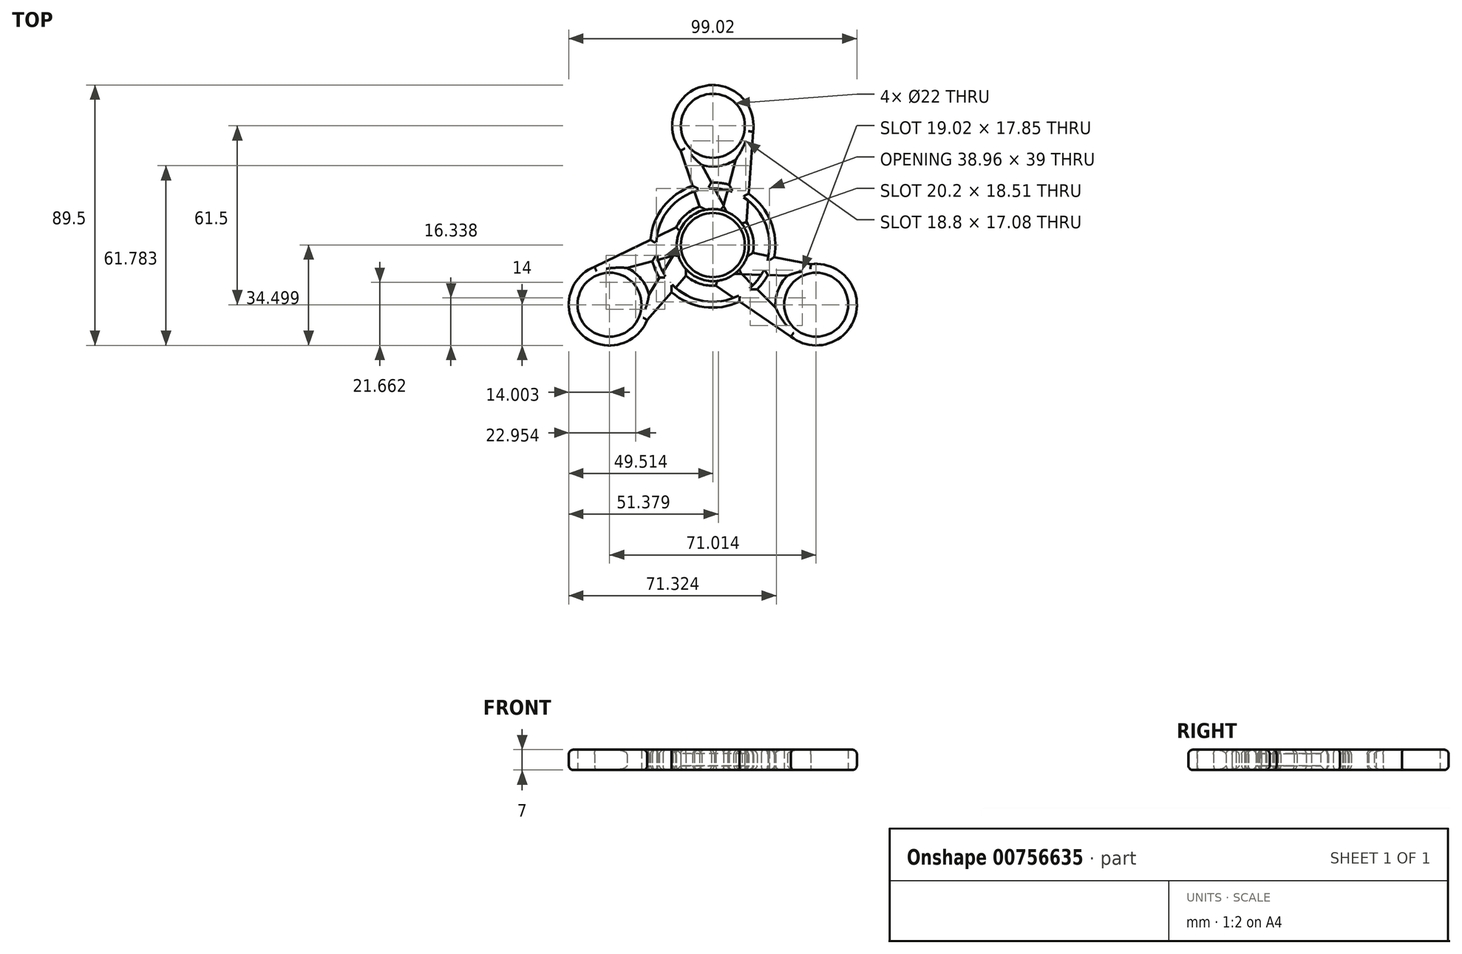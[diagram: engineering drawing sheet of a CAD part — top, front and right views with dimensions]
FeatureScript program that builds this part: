
annotation { "Feature Type Name" : "Feature", "Feature Type Description" : "" }
export const myFeature = defineFeature(function(context is Context, id is Id, definition is map)
    precondition{}
    {
        {
            var Q0;
            Q0=qCreatedBy(makeId("Top.planeOp"),FACE);
            var sketch = newSketch(context, id + "F0", { "sketchPlane" : qUnion([Q0])});
            skLineSegment(sketch, "E0.bottom", {"start": v(-14, 55) * mm, "end": v(14, 55) * mm});
            skLineSegment(sketch, "E0.top", {"start": v(-14, -14) * mm, "end": v(14, -14) * mm});
            skLineSegment(sketch, "E0.left", {"start": v(-14, 55) * mm, "end": v(-14, -14) * mm});
            skLineSegment(sketch, "E0.right", {"start": v(14, 55) * mm, "end": v(14, -14) * mm});
            skCircle(sketch, "E1", {"center": v(0, 0) * mm, "radius": 14 * mm});
            skCircle(sketch, "E2", {"center": v(0, 41) * mm, "radius": 14 * mm});
            skCircle(sketch, "E3", {"center": v(0, 0) * mm, "radius": 11 * mm});
            skCircle(sketch, "E4", {"center": v(0, 41) * mm, "radius": 11 * mm});
            skLineSegment(sketch, "E5", {"start": v(-14, 41) * mm, "end": v(14, 41) * mm});
            skLineSegment(sketch, "E6", {"start": v(-14, 0) * mm, "end": v(14, 0) * mm});
            skLineSegment(sketch, "E7", {"start": v(0, 41) * mm, "end": v(0, 0) * mm});
            skPoint(sketch, "E8", {"position": v(0, 11) * mm});
            skCircle(sketch, "E9", {"center": v(0, 0) * mm, "radius": 21.5 * mm});
            skCircle(sketch, "E10", {"center": v(0, 0) * mm, "radius": 19.5 * mm});
            skLineSegment(sketch, "E11", {"start": v(0, 21.5) * mm, "end": v(0, 19.5) * mm});
            skLineSegment(sketch, "E12", {"start": v(-14, 41) * mm, "end": v(0, 0) * mm});
            skLineSegment(sketch, "E13", {"start": v(-11, 41) * mm, "end": v(11, 0) * mm});
            skLineSegment(sketch, "E14", {"start": v(11, 41) * mm, "end": v(0, 0) * mm});
            skLineSegment(sketch, "E15", {"start": v(11, 0) * mm, "end": v(14, 41) * mm});
            skSolve(sketch);
        }
        {
            var Q0;
            {var subQ0=sQuery(id+"F0.wireOp",EDGE,"iO3ZXdYe-Cxbd-9ZMA-kq9E-F6ahPa86oXzm.right");var subQ1=sQuery(id+"F0.wireOp",EDGE,"E1");var subQ2=makeQuery(id+"F0.imprint","INTERSECT",VERTEX,{"derivedFrom":[subQ1,subQ0]});Q0=makeQuery(id+"F0.imprint","IMPRINT",FACE,{"disambiguationData":[TD([[makeQuery(id+"F0.imprint","IMPRINT",EDGE,{"disambiguationData":[TD([[subQ2,-1.0]])],"derivedFrom":subQ1}),1.0]])]});}
            var Q1;
            {var subQ0=sQuery(id+"F0.wireOp",EDGE,"E7");var subQ1=sQuery(id+"F0.wireOp",EDGE,"E2");var subQ2=makeQuery(id+"F0.imprint","INTERSECT",VERTEX,{"derivedFrom":[subQ1,subQ0]});Q1=makeQuery(id+"F0.imprint","IMPRINT",FACE,{"disambiguationData":[TD([[makeQuery(id+"F0.imprint","IMPRINT",EDGE,{"disambiguationData":[TD([[subQ2,-1.0]])],"derivedFrom":subQ1}),1.0]])]});}
            var Q2;
            {var subQ0=sQuery(id+"F0.wireOp",EDGE,"iO3ZXdYe-Cxbd-9ZMA-kq9E-F6ahPa86oXzm.right");var subQ1=sQuery(id+"F0.wireOp",EDGE,"E1");var subQ2=makeQuery(id+"F0.imprint","INTERSECT",VERTEX,{"derivedFrom":[subQ1,subQ0]});Q2=makeQuery(id+"F0.imprint","IMPRINT",FACE,{"disambiguationData":[TD([[makeQuery(id+"F0.imprint","IMPRINT",EDGE,{"disambiguationData":[TD([[subQ2,-1.0]])],"derivedFrom":subQ1}),-1.0]])]});}
            var Q3;
            {var subQ0=sQuery(id+"F0.wireOp",EDGE,"E9");var subQ1=sQuery(id+"F0.wireOp",EDGE,"iO3ZXdYe-Cxbd-9ZMA-kq9E-F6ahPa86oXzm.right");var subQ2=makeQuery(id+"F0.imprint","INTERSECT",VERTEX,{"derivedFrom":[subQ1,subQ0]});Q3=makeQuery(id+"F0.imprint","IMPRINT",FACE,{"disambiguationData":[TD([[makeQuery(id+"F0.imprint","IMPRINT",EDGE,{"disambiguationData":[TD([[subQ2,-1.0]])],"derivedFrom":subQ1}),-1.0]])]});}
            var Q4;
            {var subQ0=sQuery(id+"F0.wireOp",EDGE,"E5");var subQ3=sQuery(id+"F0.wireOp",EDGE,"E4");var subQ4=makeQuery(id+"F0.imprint","INTERSECT",VERTEX,{"disambiguationData":[OD(0.0)],"derivedFrom":[subQ3,subQ0]});Q4=makeQuery(id+"F0.imprint","IMPRINT",FACE,{"disambiguationData":[TD([[makeQuery(id+"F0.imprint","IMPRINT",EDGE,{"disambiguationData":[TD([[subQ4,1.0]])],"derivedFrom":subQ3}),-1.0]])]});}
            var Q5;
            {var subQ0=sQuery(id+"F0.wireOp",EDGE,"iO3ZXdYe-Cxbd-9ZMA-kq9E-F6ahPa86oXzm.left");var subQ1=sQuery(id+"F0.wireOp",EDGE,"E2");var subQ2=makeQuery(id+"F0.imprint","INTERSECT",VERTEX,{"derivedFrom":[subQ1,subQ0]});Q5=makeQuery(id+"F0.imprint","IMPRINT",FACE,{"disambiguationData":[TD([[makeQuery(id+"F0.imprint","IMPRINT",EDGE,{"disambiguationData":[TD([[subQ2,-1.0]])],"derivedFrom":subQ1}),1.0]])]});}
            var Q6;
            {var subQ0=sQuery(id+"F0.wireOp",EDGE,"iO3ZXdYe-Cxbd-9ZMA-kq9E-F6ahPa86oXzm.right");var subQ1=sQuery(id+"F0.wireOp",EDGE,"iO3ZXdYe-Cxbd-9ZMA-kq9E-F6ahPa86oXzm.bottom");var subQ2=makeQuery(id+"F0.imprint","INTERSECT",VERTEX,{"derivedFrom":[subQ1,subQ0]});Q6=makeQuery(id+"F0.imprint","IMPRINT",FACE,{"disambiguationData":[TD([[makeQuery(id+"F0.imprint","IMPRINT",EDGE,{"disambiguationData":[TD([[subQ2,-1.0]])],"derivedFrom":subQ0}),1.0]])]});}
            var Q7;
            {var subQ0=sQuery(id+"F0.wireOp",EDGE,"iO3ZXdYe-Cxbd-9ZMA-kq9E-F6ahPa86oXzm.left");var subQ1=sQuery(id+"F0.wireOp",EDGE,"iO3ZXdYe-Cxbd-9ZMA-kq9E-F6ahPa86oXzm.top");var subQ2=makeQuery(id+"F0.imprint","INTERSECT",VERTEX,{"derivedFrom":[subQ1,subQ0]});Q7=makeQuery(id+"F0.imprint","IMPRINT",FACE,{"disambiguationData":[TD([[makeQuery(id+"F0.imprint","IMPRINT",EDGE,{"disambiguationData":[TD([[subQ2,1.0]])],"derivedFrom":subQ0}),-1.0]])]});}
            var Q8;
            {var subQ0=sQuery(id+"F0.wireOp",EDGE,"E7");var subQ1=sQuery(id+"F0.wireOp",EDGE,"E1");var subQ2=makeQuery(id+"F0.imprint","INTERSECT",VERTEX,{"derivedFrom":[subQ1,subQ0]});Q8=makeQuery(id+"F0.imprint","IMPRINT",FACE,{"disambiguationData":[TD([[makeQuery(id+"F0.imprint","IMPRINT",EDGE,{"disambiguationData":[TD([[subQ2,-1.0]])],"derivedFrom":subQ1}),1.0]])]});}
            var Q9;
            {var subQ0=sQuery(id+"F0.wireOp",EDGE,"E6");var subQ3=sQuery(id+"F0.wireOp",EDGE,"E3");var subQ7=makeQuery(id+"F0.imprint","INTERSECT",VERTEX,{"disambiguationData":[OD(0.0)],"derivedFrom":[subQ3,subQ0]});Q9=makeQuery(id+"F0.imprint","IMPRINT",FACE,{"disambiguationData":[TD([[makeQuery(id+"F0.imprint","IMPRINT",EDGE,{"disambiguationData":[TD([[subQ7,1.0]])],"derivedFrom":subQ3}),-1.0]])]});}
            var Q10;
            {var subQ0=sQuery(id+"F0.wireOp",EDGE,"4bcde504-37b5-4423-8905-ca3e7d1b1c14");var subQ1=sQuery(id+"F0.wireOp",EDGE,"iO3ZXdYe-Cxbd-9ZMA-kq9E-F6ahPa86oXzm.left");var subQ2=makeQuery(id+"F0.imprint","INTERSECT",VERTEX,{"derivedFrom":[subQ1,subQ0]});Q10=makeQuery(id+"F0.imprint","IMPRINT",FACE,{"disambiguationData":[TD([[makeQuery(id+"F0.imprint","IMPRINT",EDGE,{"disambiguationData":[TD([[subQ2,-1.0]])],"derivedFrom":subQ1}),1.0]])]});}
            var Q11;
            {var subQ0=sQuery(id+"F0.wireOp",EDGE,"iO3ZXdYe-Cxbd-9ZMA-kq9E-F6ahPa86oXzm.left");var subQ1=sQuery(id+"F0.wireOp",EDGE,"iO3ZXdYe-Cxbd-9ZMA-kq9E-F6ahPa86oXzm.bottom");var subQ2=makeQuery(id+"F0.imprint","INTERSECT",VERTEX,{"derivedFrom":[subQ1,subQ0]});Q11=makeQuery(id+"F0.imprint","IMPRINT",FACE,{"disambiguationData":[TD([[makeQuery(id+"F0.imprint","IMPRINT",EDGE,{"disambiguationData":[TD([[subQ2,-1.0]])],"derivedFrom":subQ0}),-1.0]])]});}
            var Q12;
            {var subQ3=sQuery(id+"F0.wireOp",EDGE,"iO3ZXdYe-Cxbd-9ZMA-kq9E-F6ahPa86oXzm.top");var subQ5=sQuery(id+"F0.wireOp",EDGE,"iO3ZXdYe-Cxbd-9ZMA-kq9E-F6ahPa86oXzm.right");var subQ6=makeQuery(id+"F0.imprint","INTERSECT",VERTEX,{"derivedFrom":[subQ3,subQ5]});Q12=makeQuery(id+"F0.imprint","IMPRINT",FACE,{"disambiguationData":[TD([[makeQuery(id+"F0.imprint","IMPRINT",EDGE,{"disambiguationData":[TD([[subQ6,1.0]])],"derivedFrom":subQ5}),1.0]])]});}
            var Q13;
            {var subQ1=sQuery(id+"F0.wireOp",EDGE,"E2");var subQ3=sQuery(id+"F0.wireOp",EDGE,"iO3ZXdYe-Cxbd-9ZMA-kq9E-F6ahPa86oXzm.left");var subQ4=makeQuery(id+"F0.imprint","INTERSECT",VERTEX,{"derivedFrom":[subQ1,subQ3]});Q13=makeQuery(id+"F0.imprint","IMPRINT",FACE,{"disambiguationData":[TD([[makeQuery(id+"F0.imprint","IMPRINT",EDGE,{"disambiguationData":[TD([[subQ4,-1.0]])],"derivedFrom":subQ3}),-1.0]])]});}
            var Q14;
            {var subQ1=sQuery(id+"F0.wireOp",EDGE,"E1");var subQ3=sQuery(id+"F0.wireOp",EDGE,"iO3ZXdYe-Cxbd-9ZMA-kq9E-F6ahPa86oXzm.right");var subQ4=makeQuery(id+"F0.imprint","INTERSECT",VERTEX,{"derivedFrom":[subQ1,subQ3]});Q14=makeQuery(id+"F0.imprint","IMPRINT",FACE,{"disambiguationData":[TD([[makeQuery(id+"F0.imprint","IMPRINT",EDGE,{"disambiguationData":[TD([[subQ4,1.0]])],"derivedFrom":subQ3}),1.0]])]});}
            var Q15;
            {var subQ0=sQuery(id+"F0.wireOp",EDGE,"E9");var subQ1=sQuery(id+"F0.wireOp",EDGE,"E0.left");var subQ2=makeQuery(id+"F0.imprint","INTERSECT",VERTEX,{"derivedFrom":[subQ1,subQ0]});Q15=makeQuery(id+"F0.imprint","IMPRINT",FACE,{"disambiguationData":[TD([[makeQuery(id+"F0.imprint","IMPRINT",EDGE,{"disambiguationData":[TD([[subQ2,-1.0]])],"derivedFrom":subQ1}),1.0]])]});}
            var Q16;
            {var subQ0=sQuery(id+"F0.wireOp",EDGE,"4bcde504-37b5-4423-8905-ca3e7d1b1c14");var subQ1=sQuery(id+"F0.wireOp",EDGE,"iO3ZXdYe-Cxbd-9ZMA-kq9E-F6ahPa86oXzm.right");var subQ2=makeQuery(id+"F0.imprint","INTERSECT",VERTEX,{"derivedFrom":[subQ1,subQ0]});Q16=makeQuery(id+"F0.imprint","IMPRINT",FACE,{"disambiguationData":[TD([[makeQuery(id+"F0.imprint","IMPRINT",EDGE,{"disambiguationData":[TD([[subQ2,-1.0]])],"derivedFrom":subQ1}),1.0]])]});}
            var Q17;
            {var subQ0=sQuery(id+"F0.wireOp",EDGE,"E9");var subQ1=sQuery(id+"F0.wireOp",EDGE,"E0.right");var subQ2=makeQuery(id+"F0.imprint","INTERSECT",VERTEX,{"derivedFrom":[subQ1,subQ0]});Q17=makeQuery(id+"F0.imprint","IMPRINT",FACE,{"disambiguationData":[TD([[makeQuery(id+"F0.imprint","IMPRINT",EDGE,{"disambiguationData":[TD([[subQ2,-1.0]])],"derivedFrom":subQ1}),-1.0]])]});}
            var Q18;
            {var subQ0=sQuery(id+"F0.wireOp",EDGE,"E9");var subQ1=sQuery(id+"F0.wireOp",EDGE,"E0.left");var subQ2=makeQuery(id+"F0.imprint","INTERSECT",VERTEX,{"derivedFrom":[subQ1,subQ0]});Q18=makeQuery(id+"F0.imprint","IMPRINT",FACE,{"disambiguationData":[TD([[makeQuery(id+"F0.imprint","IMPRINT",EDGE,{"disambiguationData":[TD([[subQ2,-1.0]])],"derivedFrom":subQ1}),-1.0]])]});}
            var Q19;
            {var subQ3=sQuery(id+"F0.wireOp",EDGE,"iO3ZXdYe-Cxbd-9ZMA-kq9E-F6ahPa86oXzm.left");var subQ5=sQuery(id+"F0.wireOp",EDGE,"E9");var subQ6=makeQuery(id+"F0.imprint","INTERSECT",VERTEX,{"derivedFrom":[subQ3,subQ5]});Q19=makeQuery(id+"F0.imprint","IMPRINT",FACE,{"disambiguationData":[TD([[makeQuery(id+"F0.imprint","IMPRINT",EDGE,{"disambiguationData":[TD([[subQ6,-1.0]])],"derivedFrom":subQ3}),1.0]])]});}
            var Q20;
            {var subQ0=sQuery(id+"F0.wireOp",EDGE,"4bcde504-37b5-4423-8905-ca3e7d1b1c14");var subQ1=sQuery(id+"F0.wireOp",EDGE,"iO3ZXdYe-Cxbd-9ZMA-kq9E-F6ahPa86oXzm.right");var subQ2=makeQuery(id+"F0.imprint","INTERSECT",VERTEX,{"derivedFrom":[subQ1,subQ0]});Q20=makeQuery(id+"F0.imprint","IMPRINT",FACE,{"disambiguationData":[TD([[makeQuery(id+"F0.imprint","IMPRINT",EDGE,{"disambiguationData":[TD([[subQ2,-1.0]])],"derivedFrom":subQ1}),-1.0]])]});}
            var Q21;
            {var subQ0=sQuery(id+"F0.wireOp",EDGE,"E9");var subQ1=sQuery(id+"F0.wireOp",EDGE,"4bcde504-37b5-4423-8905-ca3e7d1b1c14");var subQ2=makeQuery(id+"F0.imprint","INTERSECT",VERTEX,{"derivedFrom":[subQ1,subQ0]});Q21=makeQuery(id+"F0.imprint","IMPRINT",FACE,{"disambiguationData":[TD([[makeQuery(id+"F0.imprint","IMPRINT",EDGE,{"disambiguationData":[TD([[subQ2,-1.0]])],"derivedFrom":subQ1}),1.0]])]});}
            var Q22;
            {var subQ0=sQuery(id+"F0.wireOp",EDGE,"E0.right");var subQ1=sQuery(id+"F0.wireOp",EDGE,"E0.top");var subQ2=makeQuery(id+"F0.imprint","INTERSECT",VERTEX,{"derivedFrom":[subQ1,subQ0]});Q22=makeQuery(id+"F0.imprint","IMPRINT",FACE,{"disambiguationData":[TD([[makeQuery(id+"F0.imprint","IMPRINT",EDGE,{"disambiguationData":[TD([[subQ2,1.0]])],"derivedFrom":subQ1}),1.0]])]});}
            var Q23;
            {var subQ0=sQuery(id+"F0.wireOp",EDGE,"E0.left");var subQ1=sQuery(id+"F0.wireOp",EDGE,"E0.top");var subQ2=makeQuery(id+"F0.imprint","INTERSECT",VERTEX,{"derivedFrom":[subQ1,subQ0]});Q23=makeQuery(id+"F0.imprint","IMPRINT",FACE,{"disambiguationData":[TD([[makeQuery(id+"F0.imprint","IMPRINT",EDGE,{"disambiguationData":[TD([[subQ2,-1.0]])],"derivedFrom":subQ1}),1.0]])]});}
            var Q24;
            {var subQ0=sQuery(id+"F0.wireOp",EDGE,"E12");var subQ2=sQuery(id+"F0.wireOp",EDGE,"E2");var subQ8=makeQuery(id+"F0.imprint","INTERSECT",VERTEX,{"derivedFrom":[subQ2,subQ0]});Q24=makeQuery(id+"F0.imprint","IMPRINT",FACE,{"disambiguationData":[TD([[makeQuery(id+"F0.imprint","IMPRINT",EDGE,{"disambiguationData":[TD([[subQ8,-1.0]])],"derivedFrom":subQ2}),1.0]])]});}
            var Q25;
            {var subQ0=sQuery(id+"F0.wireOp",EDGE,"E12");var subQ1=sQuery(id+"F0.wireOp",EDGE,"E2");var subQ3=makeQuery(id+"F0.imprint","INTERSECT",VERTEX,{"derivedFrom":[subQ1,subQ0]});Q25=makeQuery(id+"F0.imprint","IMPRINT",FACE,{"disambiguationData":[TD([[makeQuery(id+"F0.imprint","IMPRINT",EDGE,{"disambiguationData":[TD([[subQ3,1.0]])],"derivedFrom":subQ1}),1.0]])]});}
            var Q26;
            {var subQ0=sQuery(id+"F0.wireOp",EDGE,"E12");var subQ1=sQuery(id+"F0.wireOp",EDGE,"E2");var subQ2=makeQuery(id+"F0.imprint","INTERSECT",VERTEX,{"derivedFrom":[subQ1,subQ0]});Q26=makeQuery(id+"F0.imprint","IMPRINT",FACE,{"disambiguationData":[TD([[makeQuery(id+"F0.imprint","IMPRINT",EDGE,{"disambiguationData":[TD([[subQ2,-1.0]])],"derivedFrom":subQ1}),-1.0]])]});}
            var Q27;
            {var subQ1=sQuery(id+"F0.wireOp",EDGE,"E9");var subQ7=sQuery(id+"F0.wireOp",EDGE,"E13");var subQ9=makeQuery(id+"F0.imprint","INTERSECT",VERTEX,{"derivedFrom":[subQ1,subQ7]});Q27=makeQuery(id+"F0.imprint","IMPRINT",FACE,{"disambiguationData":[TD([[makeQuery(id+"F0.imprint","IMPRINT",EDGE,{"disambiguationData":[TD([[subQ9,-1.0]])],"derivedFrom":subQ1}),1.0]])]});}
            var Q28;
            {var subQ1=sQuery(id+"F0.wireOp",EDGE,"E1");var subQ3=makeQuery(id+"F0.imprint","INTERSECT",VERTEX,{"derivedFrom":[sQuery(id+"F0.wireOp",EDGE,"E0.top"),subQ1]});Q28=makeQuery(id+"F0.imprint","IMPRINT",FACE,{"disambiguationData":[TD([[makeQuery(id+"F0.imprint","IMPRINT",EDGE,{"disambiguationData":[TD([[subQ3,1.0]])],"derivedFrom":subQ1}),1.0]])]});}
            var Q29;
            {var subQ1=sQuery(id+"F0.wireOp",EDGE,"E1");var subQ3=sQuery(id+"F0.wireOp",EDGE,"E15");var subQ4=makeQuery(id+"F0.imprint","INTERSECT",VERTEX,{"derivedFrom":[subQ1,subQ3]});Q29=makeQuery(id+"F0.imprint","IMPRINT",FACE,{"disambiguationData":[TD([[makeQuery(id+"F0.imprint","IMPRINT",EDGE,{"disambiguationData":[TD([[subQ4,1.0]])],"derivedFrom":subQ1}),1.0]])]});}
            var Q30;
            {var subQ0=sQuery(id+"F0.wireOp",EDGE,"E14");var subQ1=sQuery(id+"F0.wireOp",EDGE,"E2");var subQ2=makeQuery(id+"F0.imprint","INTERSECT",VERTEX,{"derivedFrom":[subQ1,subQ0]});Q30=makeQuery(id+"F0.imprint","IMPRINT",FACE,{"disambiguationData":[TD([[makeQuery(id+"F0.imprint","IMPRINT",EDGE,{"disambiguationData":[TD([[subQ2,-1.0]])],"derivedFrom":subQ1}),-1.0]])]});}
            var Q31;
            {var subQ0=sQuery(id+"F0.wireOp",EDGE,"E15");var subQ1=sQuery(id+"F0.wireOp",EDGE,"E9");var subQ2=makeQuery(id+"F0.imprint","INTERSECT",VERTEX,{"derivedFrom":[subQ1,subQ0]});Q31=makeQuery(id+"F0.imprint","IMPRINT",FACE,{"disambiguationData":[TD([[makeQuery(id+"F0.imprint","IMPRINT",EDGE,{"disambiguationData":[TD([[subQ2,-1.0]])],"derivedFrom":subQ1}),1.0]])]});}
            var Q32;
            {var subQ5=sQuery(id+"F0.wireOp",EDGE,"E1");var subQ7=sQuery(id+"F0.wireOp",EDGE,"E15");var subQ9=makeQuery(id+"F0.imprint","INTERSECT",VERTEX,{"derivedFrom":[subQ5,subQ7]});Q32=makeQuery(id+"F0.imprint","IMPRINT",FACE,{"disambiguationData":[TD([[makeQuery(id+"F0.imprint","IMPRINT",EDGE,{"disambiguationData":[TD([[subQ9,-1.0]])],"derivedFrom":subQ5}),-1.0]])]});}
            var Q33;
            {var subQ0=sQuery(id+"F0.wireOp",EDGE,"E7");var subQ1=sQuery(id+"F0.wireOp",EDGE,"E1");var subQ2=makeQuery(id+"F0.imprint","INTERSECT",VERTEX,{"derivedFrom":[subQ1,subQ0]});Q33=makeQuery(id+"F0.imprint","IMPRINT",FACE,{"disambiguationData":[TD([[makeQuery(id+"F0.imprint","IMPRINT",EDGE,{"disambiguationData":[TD([[subQ2,-1.0]])],"derivedFrom":subQ1}),-1.0]])]});}
            var Q34;
            {var subQ3=sQuery(id+"F0.wireOp",EDGE,"E14");var subQ7=sQuery(id+"F0.wireOp",EDGE,"E1");var subQ9=makeQuery(id+"F0.imprint","INTERSECT",VERTEX,{"derivedFrom":[subQ7,subQ3]});Q34=makeQuery(id+"F0.imprint","IMPRINT",FACE,{"disambiguationData":[TD([[makeQuery(id+"F0.imprint","IMPRINT",EDGE,{"disambiguationData":[TD([[subQ9,-1.0]])],"derivedFrom":subQ7}),-1.0]])]});}
            var Q35;
            {var subQ0=sQuery(id+"F0.wireOp",EDGE,"E13");var subQ1=sQuery(id+"F0.wireOp",EDGE,"E2");var subQ2=makeQuery(id+"F0.imprint","INTERSECT",VERTEX,{"derivedFrom":[subQ1,subQ0]});Q35=makeQuery(id+"F0.imprint","IMPRINT",FACE,{"disambiguationData":[TD([[makeQuery(id+"F0.imprint","IMPRINT",EDGE,{"disambiguationData":[TD([[subQ2,-1.0]])],"derivedFrom":subQ1}),1.0]])]});}
            var Q36;
            {var subQ1=sQuery(id+"F0.wireOp",EDGE,"E10");var subQ3=sQuery(id+"F0.wireOp",EDGE,"E13");var subQ4=makeQuery(id+"F0.imprint","INTERSECT",VERTEX,{"derivedFrom":[subQ1,subQ3]});Q36=makeQuery(id+"F0.imprint","IMPRINT",FACE,{"disambiguationData":[TD([[makeQuery(id+"F0.imprint","IMPRINT",EDGE,{"disambiguationData":[TD([[subQ4,1.0]])],"derivedFrom":subQ3}),-1.0]])]});}
            extrude(context, id + "F1", {"entities" : qUnion([Q0, Q1, Q2, Q3, Q4, Q5, Q6, Q7, Q8, Q9, Q10, Q11, Q12, Q13, Q14, Q15, Q16, Q17, Q18, Q19, Q20, Q21, Q22, Q23, Q24, Q25, Q26, Q27, Q28, Q29, Q30, Q31, Q32, Q33, Q34, Q35, Q36]), "depth" : 7 * mm, "offsetDistance" : 25 * mm});
        }
        {
            var Q0;
            Q0=makeQuery(id+"F1.opExtrude","CAP_EDGE",EDGE,{"disambiguationData":[OSD([sQuery(id+"F0.wireOp",EDGE,"E9")])],"isStart":false});
            var Q1;
            {var subQ0=sQuery(id+"F0.wireOp",EDGE,"E15");Q1=makeQuery(id+"F1.opExtrude","CAP_EDGE",EDGE,{"disambiguationData":[OSD([subQ0]),TDD([makeQuery(id+"F0.imprint","IMPRINT",EDGE,{"disambiguationData":[TD([[makeQuery(id+"F0.imprint","INTERSECT",VERTEX,{"derivedFrom":[sQuery(id+"F0.wireOp",EDGE,"E2"),subQ0]}),1.0]])],"derivedFrom":subQ0})])],"isStart":false});}
            var Q2;
            Q2=makeQuery(id+"F1.opExtrude","CAP_EDGE",EDGE,{"disambiguationData":[OSD([sQuery(id+"F0.wireOp",EDGE,"E14")])],"isStart":false});
            var Q3;
            Q3=makeQuery(id+"F1.opExtrude","CAP_EDGE",EDGE,{"disambiguationData":[OSD([sQuery(id+"F0.wireOp",EDGE,"E13")])],"isStart":false});
            var Q4;
            Q4=makeQuery(id+"F1.opExtrude","CAP_EDGE",EDGE,{"disambiguationData":[OSD([sQuery(id+"F0.wireOp",EDGE,"E1")])],"isStart":false});
            var Q5;
            Q5=makeQuery(id+"F1.opExtrude","CAP_EDGE",EDGE,{"disambiguationData":[OSD([sQuery(id+"F0.wireOp",EDGE,"E9")])],"isStart":true});
            var Q6;
            Q6=makeQuery(id+"F1.opExtrude","CAP_EDGE",EDGE,{"disambiguationData":[OSD([sQuery(id+"F0.wireOp",EDGE,"E1")])],"isStart":true});
            var Q7;
            {var subQ0=sQuery(id+"F0.wireOp",EDGE,"E15");Q7=makeQuery(id+"F1.opExtrude","CAP_EDGE",EDGE,{"disambiguationData":[OSD([subQ0]),TDD([makeQuery(id+"F0.imprint","IMPRINT",EDGE,{"disambiguationData":[TD([[makeQuery(id+"F0.imprint","INTERSECT",VERTEX,{"derivedFrom":[sQuery(id+"F0.wireOp",EDGE,"E2"),subQ0]}),1.0]])],"derivedFrom":subQ0})])],"isStart":true});}
            var Q8;
            Q8=makeQuery(id+"F1.opExtrude","CAP_EDGE",EDGE,{"disambiguationData":[OSD([sQuery(id+"F0.wireOp",EDGE,"E14")])],"isStart":true});
            var Q9;
            Q9=makeQuery(id+"F1.opExtrude","CAP_EDGE",EDGE,{"disambiguationData":[OSD([sQuery(id+"F0.wireOp",EDGE,"E13")])],"isStart":true});
            var Q10;
            {var subQ0=sQuery(id+"F0.wireOp",EDGE,"E12");Q10=makeQuery(id+"F1.opExtrude","CAP_EDGE",EDGE,{"disambiguationData":[OSD([subQ0]),TDD([makeQuery(id+"F0.imprint","IMPRINT",EDGE,{"disambiguationData":[TD([[makeQuery(id+"F0.imprint","INTERSECT",VERTEX,{"derivedFrom":[sQuery(id+"F0.wireOp",EDGE,"E2"),subQ0]}),-1.0]])],"derivedFrom":subQ0})])],"isStart":false});}
            var Q11;
            {var subQ0=sQuery(id+"F0.wireOp",EDGE,"E12");Q11=makeQuery(id+"F1.opExtrude","CAP_EDGE",EDGE,{"disambiguationData":[OSD([subQ0]),TDD([makeQuery(id+"F0.imprint","IMPRINT",EDGE,{"disambiguationData":[TD([[makeQuery(id+"F0.imprint","INTERSECT",VERTEX,{"derivedFrom":[sQuery(id+"F0.wireOp",EDGE,"E2"),subQ0]}),-1.0]])],"derivedFrom":subQ0})])],"isStart":true});}
            var Q12;
            {var subQ0=sQuery(id+"F0.wireOp",EDGE,"E12");Q12=makeQuery(id+"F1.opExtrude","CAP_EDGE",EDGE,{"disambiguationData":[OSD([subQ0]),TDD([makeQuery(id+"F0.imprint","IMPRINT",EDGE,{"disambiguationData":[TD([[makeQuery(id+"F0.imprint","INTERSECT",VERTEX,{"derivedFrom":[sQuery(id+"F0.wireOp",EDGE,"E1"),subQ0]}),1.0]])],"derivedFrom":subQ0})])],"isStart":false});}
            var Q13;
            {var subQ0=sQuery(id+"F0.wireOp",EDGE,"E15");Q13=makeQuery(id+"F1.opExtrude","CAP_EDGE",EDGE,{"disambiguationData":[OSD([subQ0]),TDD([makeQuery(id+"F0.imprint","IMPRINT",EDGE,{"disambiguationData":[TD([[makeQuery(id+"F0.imprint","INTERSECT",VERTEX,{"derivedFrom":[sQuery(id+"F0.wireOp",EDGE,"E1"),subQ0]}),-1.0]])],"derivedFrom":subQ0})])],"isStart":false});}
            var Q14;
            {var subQ0=sQuery(id+"F0.wireOp",EDGE,"E12");Q14=makeQuery(id+"F1.opExtrude","CAP_EDGE",EDGE,{"disambiguationData":[OSD([subQ0]),TDD([makeQuery(id+"F0.imprint","IMPRINT",EDGE,{"disambiguationData":[TD([[makeQuery(id+"F0.imprint","INTERSECT",VERTEX,{"derivedFrom":[sQuery(id+"F0.wireOp",EDGE,"E1"),subQ0]}),1.0]])],"derivedFrom":subQ0})])],"isStart":true});}
            var Q15;
            {var subQ0=sQuery(id+"F0.wireOp",EDGE,"E15");Q15=makeQuery(id+"F1.opExtrude","CAP_EDGE",EDGE,{"disambiguationData":[OSD([subQ0]),TDD([makeQuery(id+"F0.imprint","IMPRINT",EDGE,{"disambiguationData":[TD([[makeQuery(id+"F0.imprint","INTERSECT",VERTEX,{"derivedFrom":[sQuery(id+"F0.wireOp",EDGE,"E1"),subQ0]}),-1.0]])],"derivedFrom":subQ0})])],"isStart":true});}
            var Q16;
            {var subQ0=sQuery(id+"F0.wireOp",EDGE,"E15");var subQ2=sQuery(id+"F0.wireOp",EDGE,"E2");var subQ4=sQuery(id+"F0.wireOp",EDGE,"E12");var subQ6=makeQuery(id+"F0.imprint","INTERSECT",VERTEX,{"derivedFrom":[sQuery(id+"F0.wireOp",EDGE,"E0.bottom"),subQ2]});Q16=makeQuery(id+"F1.opExtrude","CAP_EDGE",EDGE,{"disambiguationData":[OSD([subQ2]),TDD([makeQuery(id+"F0.imprint","IMPRINT",EDGE,{"disambiguationData":[TD([[subQ6,1.0]])],"derivedFrom":subQ2}),makeQuery(id+"F0.imprint","IMPRINT",EDGE,{"disambiguationData":[TD([[subQ6,-1.0]])],"derivedFrom":subQ2}),makeQuery(id+"F0.imprint","IMPRINT",EDGE,{"disambiguationData":[TD([[makeQuery(id+"F0.imprint","INTERSECT",VERTEX,{"derivedFrom":[subQ2,subQ4]}),1.0]])],"derivedFrom":subQ2}),makeQuery(id+"F0.imprint","IMPRINT",EDGE,{"disambiguationData":[TD([[makeQuery(id+"F0.imprint","INTERSECT",VERTEX,{"derivedFrom":[subQ2,subQ0]}),-1.0]])],"derivedFrom":subQ2})])],"isStart":false});}
            var Q17;
            {var subQ0=sQuery(id+"F0.wireOp",EDGE,"E15");var subQ2=sQuery(id+"F0.wireOp",EDGE,"E2");var subQ4=sQuery(id+"F0.wireOp",EDGE,"E12");var subQ6=makeQuery(id+"F0.imprint","INTERSECT",VERTEX,{"derivedFrom":[sQuery(id+"F0.wireOp",EDGE,"E0.bottom"),subQ2]});Q17=makeQuery(id+"F1.opExtrude","CAP_EDGE",EDGE,{"disambiguationData":[OSD([subQ2]),TDD([makeQuery(id+"F0.imprint","IMPRINT",EDGE,{"disambiguationData":[TD([[subQ6,1.0]])],"derivedFrom":subQ2}),makeQuery(id+"F0.imprint","IMPRINT",EDGE,{"disambiguationData":[TD([[subQ6,-1.0]])],"derivedFrom":subQ2}),makeQuery(id+"F0.imprint","IMPRINT",EDGE,{"disambiguationData":[TD([[makeQuery(id+"F0.imprint","INTERSECT",VERTEX,{"derivedFrom":[subQ2,subQ4]}),1.0]])],"derivedFrom":subQ2}),makeQuery(id+"F0.imprint","IMPRINT",EDGE,{"disambiguationData":[TD([[makeQuery(id+"F0.imprint","INTERSECT",VERTEX,{"derivedFrom":[subQ2,subQ0]}),-1.0]])],"derivedFrom":subQ2})])],"isStart":true});}
            var Q18;
            {var subQ0=sQuery(id+"F0.wireOp",EDGE,"E2");var subQ1=makeQuery(id+"F0.imprint","INTERSECT",VERTEX,{"derivedFrom":[subQ0,sQuery(id+"F0.wireOp",EDGE,"E7")]});Q18=makeQuery(id+"F1.opExtrude","CAP_EDGE",EDGE,{"disambiguationData":[OSD([subQ0]),TDD([makeQuery(id+"F0.imprint","IMPRINT",EDGE,{"disambiguationData":[TD([[makeQuery(id+"F0.imprint","INTERSECT",VERTEX,{"derivedFrom":[subQ0,sQuery(id+"F0.wireOp",EDGE,"E13")]}),-1.0]])],"derivedFrom":subQ0}),makeQuery(id+"F0.imprint","IMPRINT",EDGE,{"disambiguationData":[TD([[subQ1,-1.0]])],"derivedFrom":subQ0})])],"isStart":true});}
            var Q19;
            {var subQ0=sQuery(id+"F0.wireOp",EDGE,"E2");var subQ1=makeQuery(id+"F0.imprint","INTERSECT",VERTEX,{"derivedFrom":[subQ0,sQuery(id+"F0.wireOp",EDGE,"E7")]});Q19=makeQuery(id+"F1.opExtrude","CAP_EDGE",EDGE,{"disambiguationData":[OSD([subQ0]),TDD([makeQuery(id+"F0.imprint","IMPRINT",EDGE,{"disambiguationData":[TD([[makeQuery(id+"F0.imprint","INTERSECT",VERTEX,{"derivedFrom":[subQ0,sQuery(id+"F0.wireOp",EDGE,"E13")]}),-1.0]])],"derivedFrom":subQ0}),makeQuery(id+"F0.imprint","IMPRINT",EDGE,{"disambiguationData":[TD([[subQ1,-1.0]])],"derivedFrom":subQ0})])],"isStart":false});}
            fillet(context, id + "F2", {"entities" : qUnion([Q0, Q1, Q2, Q3, Q4, Q5, Q6, Q7, Q8, Q9, Q10, Q11, Q12, Q13, Q14, Q15, Q16, Q17, Q18, Q19]), "radius" : 1.6 * mm, "tangentPropagation" : true, "allowEdgeOverflow" : false});
        }
        {
            var Q0;
            Q0=makeQuery(id+"F1.opExtrude","SWEPT_BODY",BODY,{"disambiguationData":[OSD([sQuery(id+"F0.wireOp",EDGE,"E0.left"),sQuery(id+"F0.wireOp",EDGE,"E0.right"),sQuery(id+"F0.wireOp",EDGE,"E1"),sQuery(id+"F0.wireOp",EDGE,"E2"),sQuery(id+"F0.wireOp",EDGE,"E3"),sQuery(id+"F0.wireOp",EDGE,"E4")])]});
            var Q1;
            Q1=makeQuery(id+"F1.opExtrude","SWEPT_FACE",FACE,{"disambiguationData":[OSD([sQuery(id+"F0.wireOp",EDGE,"E3")])]});
            circularPattern(context, id + "F3", {"entities" : qUnion([Q0]), "axis" : qUnion([Q1]), "angle" : 360 * degree, "instanceCount" : 3, "equalSpace" : true});
        }
        {
            var Q0;
            Q0=makeQuery(id+"F3.opPattern","COPY",BODY,{"derivedFrom":makeQuery(id+"F1.opExtrude","SWEPT_BODY",BODY,{"disambiguationData":[OSD([sQuery(id+"F0.wireOp",EDGE,"E0.left"),sQuery(id+"F0.wireOp",EDGE,"E0.right"),sQuery(id+"F0.wireOp",EDGE,"E1"),sQuery(id+"F0.wireOp",EDGE,"E2"),sQuery(id+"F0.wireOp",EDGE,"E3"),sQuery(id+"F0.wireOp",EDGE,"E4")])]}),"instanceName":"2"});
            var Q1;
            Q1=makeQuery(id+"F3.opPattern","COPY",BODY,{"derivedFrom":makeQuery(id+"F1.opExtrude","SWEPT_BODY",BODY,{"disambiguationData":[OSD([sQuery(id+"F0.wireOp",EDGE,"E0.left"),sQuery(id+"F0.wireOp",EDGE,"E0.right"),sQuery(id+"F0.wireOp",EDGE,"E1"),sQuery(id+"F0.wireOp",EDGE,"E2"),sQuery(id+"F0.wireOp",EDGE,"E3"),sQuery(id+"F0.wireOp",EDGE,"E4")])]}),"instanceName":"1"});
            var Q2;
            Q2=makeQuery(id+"F1.opExtrude","SWEPT_BODY",BODY,{"disambiguationData":[OSD([sQuery(id+"F0.wireOp",EDGE,"E0.left"),sQuery(id+"F0.wireOp",EDGE,"E0.right"),sQuery(id+"F0.wireOp",EDGE,"E1"),sQuery(id+"F0.wireOp",EDGE,"E2"),sQuery(id+"F0.wireOp",EDGE,"E3"),sQuery(id+"F0.wireOp",EDGE,"E4")])]});
            booleanBodies(context, id + "F4", {"operationType" : BooleanOperationType.UNION, "tools" : qUnion([Q0, Q1, Q2])});
        }
        {
            var Q0;
            {var subQ0=makeQuery(id+"F1.opExtrude","CAP_EDGE",EDGE,{"disambiguationData":[OSD([sQuery(id+"F0.wireOp",EDGE,"E3")])],"isStart":true});Q0=makeQuery(id+"F4.opBoolean","MERGE",EDGE,{"derivedFrom":[subQ0,makeQuery(id+"F3.opPattern","COPY",EDGE,{"derivedFrom":subQ0,"instanceName":"1"}),makeQuery(id+"F3.opPattern","COPY",EDGE,{"derivedFrom":subQ0,"instanceName":"2"})]});}
            var Q1;
            {var subQ0=makeQuery(id+"F1.opExtrude","CAP_EDGE",EDGE,{"disambiguationData":[OSD([sQuery(id+"F0.wireOp",EDGE,"E3")])],"isStart":false});Q1=makeQuery(id+"F4.opBoolean","MERGE",EDGE,{"derivedFrom":[subQ0,makeQuery(id+"F3.opPattern","COPY",EDGE,{"derivedFrom":subQ0,"instanceName":"1"}),makeQuery(id+"F3.opPattern","COPY",EDGE,{"derivedFrom":subQ0,"instanceName":"2"})]});}
            chamfer(context, id + "F5", {"entities" : qUnion([Q0, Q1]), "width" : 1.4 * mm, "tangentPropagation" : true});
        }
    });
